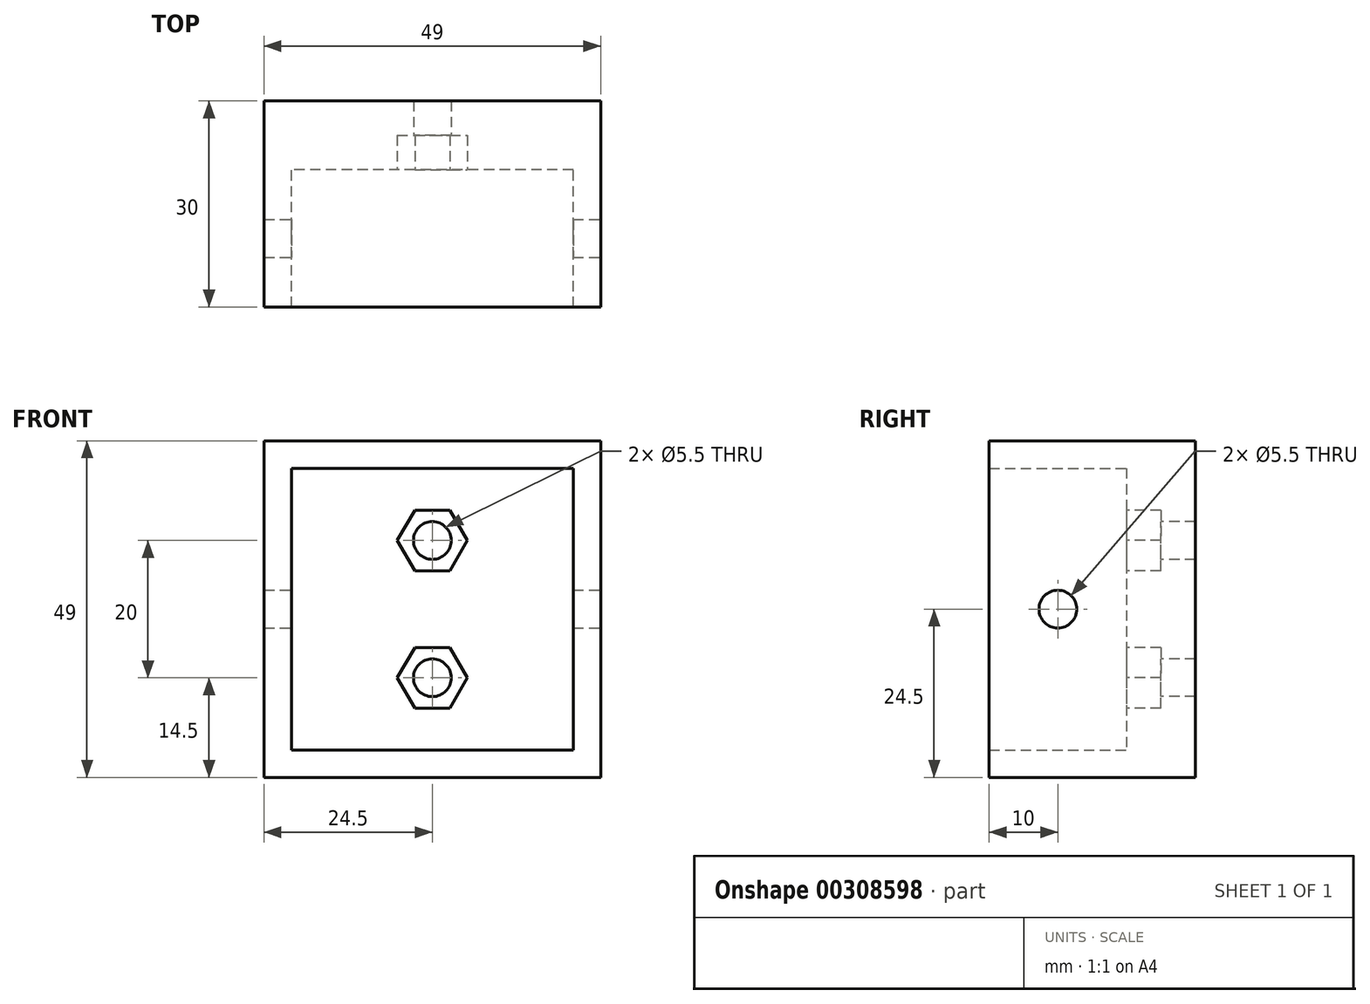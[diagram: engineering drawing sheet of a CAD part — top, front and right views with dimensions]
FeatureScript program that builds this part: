
annotation { "Feature Type Name" : "Feature", "Feature Type Description" : "" }
export const myFeature = defineFeature(function(context is Context, id is Id, definition is map)
    precondition{}
    {
        {
            var Q0;
            Q0=qCreatedBy(makeId("Front.planeOp"),FACE);
            var sketch = newSketch(context, id + "F0", { "sketchPlane" : qUnion([Q0])});
            skLineSegment(sketch, "E0.bottom", {"start": v(20.5, 20.5) * mm, "end": v(-20.5, 20.5) * mm});
            skLineSegment(sketch, "E0.top", {"start": v(20.5, -20.5) * mm, "end": v(-20.5, -20.5) * mm});
            skLineSegment(sketch, "E0.left", {"start": v(20.5, 20.5) * mm, "end": v(20.5, -20.5) * mm});
            skLineSegment(sketch, "E0.right", {"start": v(-20.5, 20.5) * mm, "end": v(-20.5, -20.5) * mm});
            skPoint(sketch, "E0.middle", {"position": v(0, 0) * mm});
            skLineSegment(sketch, "E1.0", {"start": v(-24.5, 24.5) * mm, "end": v(-24.5, -24.5) * mm});
            skLineSegment(sketch, "E1.1", {"start": v(24.5, 24.5) * mm, "end": v(-24.5, 24.5) * mm});
            skLineSegment(sketch, "E1.2", {"start": v(24.5, 24.5) * mm, "end": v(24.5, -24.5) * mm});
            skLineSegment(sketch, "E1.3", {"start": v(24.5, -24.5) * mm, "end": v(-24.5, -24.5) * mm});
            skPoint(sketch, "E2", {"position": v(0, 10) * mm});
            skPoint(sketch, "E3", {"position": v(0, -10) * mm});
            skSolve(sketch);
        }
        {
            var Q0;
            Q0=makeQuery(id+"F0.imprint","IMPRINT",FACE,{"disambiguationData":[TD([[makeQuery(id+"F0.imprint","IMPRINT",EDGE,{"derivedFrom":sQuery(id+"F0.wireOp",EDGE,"E0.bottom")}),-1.0]])]});
            extrude(context, id + "F1", {"entities" : qUnion([Q0]), "depth" : 20 * mm});
        }
        {
            var Q0;
            Q0=makeQuery(id+"F0.imprint","IMPRINT",FACE,{"disambiguationData":[TD([[makeQuery(id+"F0.imprint","IMPRINT",EDGE,{"derivedFrom":sQuery(id+"F0.wireOp",EDGE,"E0.bottom")}),1.0]])]});
            var Q1;
            Q1=makeQuery(id+"F0.imprint","IMPRINT",FACE,{"disambiguationData":[TD([[makeQuery(id+"F0.imprint","IMPRINT",EDGE,{"derivedFrom":sQuery(id+"F0.wireOp",EDGE,"E0.bottom")}),-1.0]])]});
            extrude(context, id + "F2", {"entities" : qUnion([Q0, Q1]), "operationType" : NewBodyOperationType.ADD, "oppositeDirection" : true, "depth" : 10 * mm});
        }
        {
            var Q0;
            Q0=sQuery(id+"F0.wireOp",VERTEX,"E2");
            var Q1;
            Q1=sQuery(id+"F0.wireOp",VERTEX,"E3");
            var Q2;
            Q2=makeQuery(id+"F1.opExtrude","SWEPT_BODY",BODY,{"disambiguationData":[OSD([sQuery(id+"F0.wireOp",EDGE,"E0.bottom"),sQuery(id+"F0.wireOp",EDGE,"E0.top"),sQuery(id+"F0.wireOp",EDGE,"E0.left"),sQuery(id+"F0.wireOp",EDGE,"E0.right"),sQuery(id+"F0.wireOp",EDGE,"E1.0"),sQuery(id+"F0.wireOp",EDGE,"E1.1"),sQuery(id+"F0.wireOp",EDGE,"E1.2"),sQuery(id+"F0.wireOp",EDGE,"E1.3")])]});
            hole(context, id + "F3", {"style" : HoleStyle.SIMPLE, "endStyle" : HoleEndStyle.THROUGH, "holeDiameter" : 5.5 * mm, "tappedDepth" : 12 * mm, "tapClearance" : 3, "locations" : qUnion([Q0, Q1]), "scope" : qUnion([Q2])});
        }
        {
            var Q0;
            {var subQ0=sQuery(id+"F0.wireOp",EDGE,"E1.2");Q0=makeQuery(id+"F2.boolean.opBoolean","MERGE",FACE,{"derivedFrom":[makeQuery(id+"F1.opExtrude","SWEPT_FACE",FACE,{"disambiguationData":[OSD([subQ0])]}),makeQuery(id+"F2.opExtrude","SWEPT_FACE",FACE,{"disambiguationData":[OSD([subQ0])]})]});}
            var sketch = newSketch(context, id + "F4", { "sketchPlane" : qUnion([Q0])});
            skPoint(sketch, "E4", {"position": v(-10, 0) * mm});
            skSolve(sketch);
        }
        {
            var Q0;
            Q0=sQuery(id+"F4.wireOp",VERTEX,"E4");
            var Q1;
            Q1=makeQuery(id+"F1.opExtrude","SWEPT_BODY",BODY,{"disambiguationData":[OSD([sQuery(id+"F0.wireOp",EDGE,"E0.bottom"),sQuery(id+"F0.wireOp",EDGE,"E0.top"),sQuery(id+"F0.wireOp",EDGE,"E0.left"),sQuery(id+"F0.wireOp",EDGE,"E0.right"),sQuery(id+"F0.wireOp",EDGE,"E1.0"),sQuery(id+"F0.wireOp",EDGE,"E1.1"),sQuery(id+"F0.wireOp",EDGE,"E1.2"),sQuery(id+"F0.wireOp",EDGE,"E1.3")])]});
            hole(context, id + "F5", {"style" : HoleStyle.SIMPLE, "endStyle" : HoleEndStyle.THROUGH, "holeDiameter" : 5.5 * mm, "tappedDepth" : 12 * mm, "tapClearance" : 3, "locations" : qUnion([Q0]), "scope" : qUnion([Q1])});
        }
        {
            var Q0;
            Q0=makeQuery(id+"F0.imprint","IMPRINT",FACE,{"disambiguationData":[TD([[makeQuery(id+"F0.imprint","IMPRINT",EDGE,{"derivedFrom":sQuery(id+"F0.wireOp",EDGE,"E0.bottom")}),1.0]])]});
            var sketch = newSketch(context, id + "F6", { "sketchPlane" : qUnion([Q0])});
            skCircle(sketch, "E5.cCircle", {"center": v(0, 10) * mm, "radius": 4.42 * mm, "construction": true});
            skLineSegment(sketch, "E5.0", {"start": v(2.55, 14.42) * mm, "end": v(5.1, 10) * mm});
            skLineSegment(sketch, "E5.1", {"start": v(5.1, 10) * mm, "end": v(2.55, 5.58) * mm});
            skLineSegment(sketch, "E5.2", {"start": v(2.55, 5.58) * mm, "end": v(-2.55, 5.58) * mm});
            skLineSegment(sketch, "E5.3", {"start": v(-2.55, 5.58) * mm, "end": v(-5.1, 10) * mm});
            skLineSegment(sketch, "E5.4", {"start": v(-5.1, 10) * mm, "end": v(-2.55, 14.42) * mm});
            skLineSegment(sketch, "E5.5", {"start": v(-2.55, 14.42) * mm, "end": v(2.55, 14.42) * mm});
            skPoint(sketch, "E5.0.midPoint", {"position": v(3.82, 12.2) * mm});
            skCircle(sketch, "E6.cCircle", {"center": v(0, -10) * mm, "radius": 4.42 * mm, "construction": true});
            skLineSegment(sketch, "E6.0", {"start": v(2.55, -5.58) * mm, "end": v(5.1, -10) * mm});
            skLineSegment(sketch, "E6.1", {"start": v(5.1, -10) * mm, "end": v(2.55, -14.42) * mm});
            skLineSegment(sketch, "E6.2", {"start": v(2.55, -14.42) * mm, "end": v(-2.55, -14.42) * mm});
            skLineSegment(sketch, "E6.3", {"start": v(-2.55, -14.42) * mm, "end": v(-5.1, -10) * mm});
            skLineSegment(sketch, "E6.4", {"start": v(-5.1, -10) * mm, "end": v(-2.55, -5.58) * mm});
            skLineSegment(sketch, "E6.5", {"start": v(-2.55, -5.58) * mm, "end": v(2.55, -5.58) * mm});
            skPoint(sketch, "E6.0.midPoint", {"position": v(3.83, -7.8) * mm});
            skSolve(sketch);
        }
        {
            var Q0;
            Q0=makeQuery(id+"F6.imprint","IMPRINT",FACE,{"disambiguationData":[TD([[makeQuery(id+"F6.imprint","IMPRINT",EDGE,{"derivedFrom":sQuery(id+"F6.wireOp",EDGE,"E5.0")}),-1.0]])]});
            var Q1;
            Q1=makeQuery(id+"F6.imprint","IMPRINT",FACE,{"disambiguationData":[TD([[makeQuery(id+"F6.imprint","IMPRINT",EDGE,{"derivedFrom":sQuery(id+"F6.wireOp",EDGE,"E6.0")}),-1.0]])]});
            var Q2;
            Q2=sQuery(id+"F6.wireOp",EDGE,"E5.2");
            var Q3;
            Q3=sQuery(id+"F6.wireOp",EDGE,"E5.1");
            var Q4;
            Q4=sQuery(id+"F6.wireOp",EDGE,"E5.0");
            var Q5;
            Q5=sQuery(id+"F6.wireOp",EDGE,"E5.4");
            var Q6;
            Q6=sQuery(id+"F6.wireOp",EDGE,"E5.5");
            var Q7;
            Q7=sQuery(id+"F6.wireOp",EDGE,"E5.3");
            var Q8;
            Q8=sQuery(id+"F6.wireOp",EDGE,"E6.5");
            var Q9;
            Q9=sQuery(id+"F6.wireOp",EDGE,"E6.0");
            var Q10;
            Q10=sQuery(id+"F6.wireOp",EDGE,"E6.1");
            var Q11;
            Q11=sQuery(id+"F6.wireOp",EDGE,"E6.2");
            var Q12;
            Q12=sQuery(id+"F6.wireOp",EDGE,"E6.3");
            var Q13;
            Q13=sQuery(id+"F6.wireOp",EDGE,"E6.4");
            extrude(context, id + "F7", {"entities" : qUnion([Q0, Q1]), "surfaceEntities" : qUnion([Q2, Q3, Q4, Q5, Q6, Q7, Q8, Q9, Q10, Q11, Q12, Q13]), "oppositeDirection" : true, "depth" : 5 * mm});
        }
        {
            var Q0;
            Q0=makeQuery(id+"F7.opExtrude","SWEPT_BODY",BODY,{"disambiguationData":[OSD([sQuery(id+"F6.wireOp",EDGE,"E5.0"),sQuery(id+"F6.wireOp",EDGE,"E5.1"),sQuery(id+"F6.wireOp",EDGE,"E5.2"),sQuery(id+"F6.wireOp",EDGE,"E5.3"),sQuery(id+"F6.wireOp",EDGE,"E5.4"),sQuery(id+"F6.wireOp",EDGE,"E5.5")])]});
            var Q1;
            Q1=makeQuery(id+"F7.opExtrude","SWEPT_BODY",BODY,{"disambiguationData":[OSD([sQuery(id+"F6.wireOp",EDGE,"E6.0"),sQuery(id+"F6.wireOp",EDGE,"E6.1"),sQuery(id+"F6.wireOp",EDGE,"E6.2"),sQuery(id+"F6.wireOp",EDGE,"E6.3"),sQuery(id+"F6.wireOp",EDGE,"E6.4"),sQuery(id+"F6.wireOp",EDGE,"E6.5")])]});
            var Q2;
            Q2=makeQuery(id+"F1.opExtrude","SWEPT_BODY",BODY,{"disambiguationData":[OSD([sQuery(id+"F0.wireOp",EDGE,"E0.bottom"),sQuery(id+"F0.wireOp",EDGE,"E0.top"),sQuery(id+"F0.wireOp",EDGE,"E0.left"),sQuery(id+"F0.wireOp",EDGE,"E0.right"),sQuery(id+"F0.wireOp",EDGE,"E1.0"),sQuery(id+"F0.wireOp",EDGE,"E1.1"),sQuery(id+"F0.wireOp",EDGE,"E1.2"),sQuery(id+"F0.wireOp",EDGE,"E1.3")])]});
            booleanBodies(context, id + "F8", {"operationType" : BooleanOperationType.SUBTRACTION, "tools" : qUnion([Q0, Q1]), "targets" : qUnion([Q2])});
        }
    });
